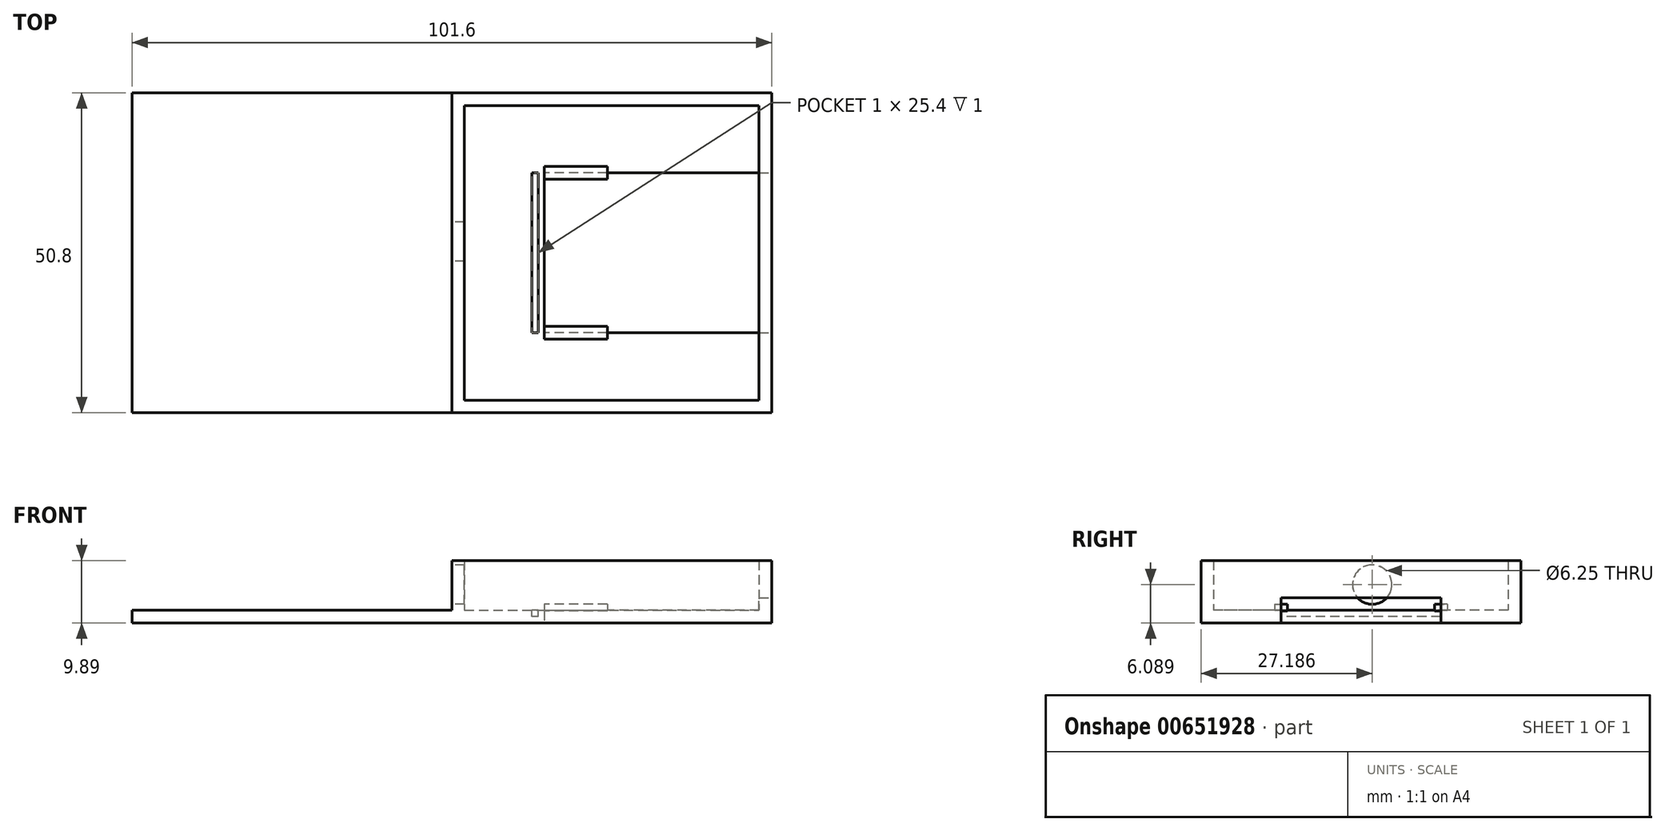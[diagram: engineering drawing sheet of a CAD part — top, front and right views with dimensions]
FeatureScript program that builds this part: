
annotation { "Feature Type Name" : "Feature", "Feature Type Description" : "" }
export const myFeature = defineFeature(function(context is Context, id is Id, definition is map)
    precondition{}
    {
        {
            var Q0;
            Q0=qCreatedBy(makeId("Top.planeOp"),FACE);
            var sketch = newSketch(context, id + "F0", { "sketchPlane" : qUnion([Q0])});
            skLineSegment(sketch, "E0.bottom", {"start": v(-50.8, 25.4) * mm, "end": v(50.8, 25.4) * mm});
            skLineSegment(sketch, "E0.top", {"start": v(-50.8, -25.4) * mm, "end": v(50.8, -25.4) * mm});
            skLineSegment(sketch, "E0.right", {"start": v(50.8, 25.4) * mm, "end": v(50.8, 12.7) * mm});
            skPoint(sketch, "E1.start.orphan", {"position": v(-50.8, 0) * mm});
            skLineSegment(sketch, "E2", {"start": v(-50.8, 25.4) * mm, "end": v(-50.8, -25.4) * mm});
            skLineSegment(sketch, "E3", {"start": v(50.8, 12.7) * mm, "end": v(14.7, 12.7) * mm});
            skLineSegment(sketch, "E4.MirrorCS", {"start": v(50.8, -12.7) * mm, "end": v(14.7, -12.7) * mm});
            skLineSegment(sketch, "E5.trimOffspring", {"start": v(50.8, -12.7) * mm, "end": v(50.8, -25.4) * mm});
            skLineSegment(sketch, "E6", {"start": v(14.7, -12.7) * mm, "end": v(14.7, 12.7) * mm});
            skSolve(sketch);
        }
        {
            var Q0;
            Q0 = qSketchRegion(id + "F0", true);
            extrude(context, id + "F1", {"entities" : qUnion([Q0]), "depth" : 2 * mm, "offsetDistance" : 25.4 * mm});
        }
        {
            var Q0;
            Q0=makeQuery(id+"F1.opExtrude","CAP_FACE",FACE,{"disambiguationData":[OSD([sQuery(id+"F0.wireOp",EDGE,"E0.bottom"),sQuery(id+"F0.wireOp",EDGE,"E0.top"),sQuery(id+"F0.wireOp",EDGE,"E0.right"),sQuery(id+"F0.wireOp",EDGE,"E2")])],"isStart":false});
            var sketch = newSketch(context, id + "F2", { "sketchPlane" : qUnion([Q0])});
            skLineSegment(sketch, "E7", {"start": v(50.8, 25.4) * mm, "end": v(0, 25.4) * mm});
            skLineSegment(sketch, "E8", {"start": v(2, 23.4) * mm, "end": v(48.8, 23.4) * mm});
            skLineSegment(sketch, "E9", {"start": v(48.8, 23.4) * mm, "end": v(48.8, -23.4) * mm});
            skLineSegment(sketch, "E10", {"start": v(48.8, -23.4) * mm, "end": v(2, -23.4) * mm});
            skLineSegment(sketch, "E11", {"start": v(0, -25.4) * mm, "end": v(50.8, -25.4) * mm});
            skLineSegment(sketch, "E12", {"start": v(50.8, -25.4) * mm, "end": v(50.8, 25.4) * mm});
            skLineSegment(sketch, "E13", {"start": v(0, 25.4) * mm, "end": v(0, -25.4) * mm});
            skLineSegment(sketch, "E14.0", {"start": v(2, 23.4) * mm, "end": v(2, -23.4) * mm});
            skPoint(sketch, "E15.orphan", {"position": v(0, -23.4) * mm});
            skSolve(sketch);
        }
        {
            var Q0;
            Q0 = qSketchRegion(id + "F2", true);
            extrude(context, id + "F3", {"entities" : qUnion([Q0]), "operationType" : NewBodyOperationType.ADD, "depth" : 8.9 * mm, "offsetDistance" : 25.4 * mm});
        }
        {
            var Q0;
            Q0=makeQuery(id+"F3.opExtrude","SWEPT_FACE",FACE,{"disambiguationData":[OSD([sQuery(id+"F2.wireOp",EDGE,"E13")])]});
            var sketch = newSketch(context, id + "F4", { "sketchPlane" : qUnion([Q0])});
            skCircle(sketch, "E16", {"center": v(-1.79, 6.09) * mm, "radius": 3.13 * mm});
            skSolve(sketch);
        }
        {
            var Q0;
            Q0 = qSketchRegion(id + "F4", true);
            extrude(context, id + "F5", {"entities" : qUnion([Q0]), "operationType" : NewBodyOperationType.REMOVE, "oppositeDirection" : true, "depth" : 25.4 * mm, "offsetDistance" : 25.4 * mm});
        }
        {
            var Q0;
            Q0=makeQuery(id+"F3.boolean.opBoolean","MERGE",FACE,{"derivedFrom":[makeQuery(id+"F1.opExtrude","SWEPT_FACE",FACE,{"disambiguationData":[OSD([sQuery(id+"F0.wireOp",EDGE,"E0.right")])]}),makeQuery(id+"F1.opExtrude","SWEPT_FACE",FACE,{"disambiguationData":[OSD([sQuery(id+"F0.wireOp",EDGE,"E5.trimOffspring")])]}),makeQuery(id+"F3.opExtrude","SWEPT_FACE",FACE,{"disambiguationData":[OSD([sQuery(id+"F2.wireOp",EDGE,"E12")])]})]});
            var sketch = newSketch(context, id + "F6", { "sketchPlane" : qUnion([Q0])});
            skLineSegment(sketch, "E17.bottom", {"start": v(12.7, 2) * mm, "end": v(-12.7, 2) * mm});
            skLineSegment(sketch, "E17.top", {"start": v(12.7, 4) * mm, "end": v(-12.7, 4) * mm});
            skLineSegment(sketch, "E17.left", {"start": v(12.7, 2) * mm, "end": v(12.7, 4) * mm});
            skLineSegment(sketch, "E17.right", {"start": v(-12.7, 2) * mm, "end": v(-12.7, 4) * mm});
            skSolve(sketch);
        }
        {
            var Q0;
            Q0 = qSketchRegion(id + "F6", true);
            extrude(context, id + "F7", {"entities" : qUnion([Q0]), "operationType" : NewBodyOperationType.REMOVE, "oppositeDirection" : true, "depth" : 25.4 * mm, "offsetDistance" : 25.4 * mm});
        }
        {
            var Q0;
            Q0=makeQuery(id+"F3.opExtrude","CAP_FACE",FACE,{"disambiguationData":[OSD([sQuery(id+"F2.wireOp",EDGE,"E7"),sQuery(id+"F2.wireOp",EDGE,"E8"),sQuery(id+"F2.wireOp",EDGE,"E9"),sQuery(id+"F2.wireOp",EDGE,"E10"),sQuery(id+"F2.wireOp",EDGE,"E11"),sQuery(id+"F2.wireOp",EDGE,"E12"),sQuery(id+"F2.wireOp",EDGE,"E13"),sQuery(id+"F2.wireOp",EDGE,"E14.0")])],"isStart":false});
            var sketch = newSketch(context, id + "F8", { "sketchPlane" : qUnion([Q0])});
            skLineSegment(sketch, "E18.bottom", {"start": v(0, 25.4) * mm, "end": v(50.8, 25.4) * mm});
            skLineSegment(sketch, "E18.top", {"start": v(0, -25.4) * mm, "end": v(50.8, -25.4) * mm});
            skLineSegment(sketch, "E18.left", {"start": v(0, 25.4) * mm, "end": v(0, -25.4) * mm});
            skLineSegment(sketch, "E18.right", {"start": v(50.8, 25.4) * mm, "end": v(50.8, -25.4) * mm});
            skSolve(sketch);
        }
        {
            var Q0;
            Q0 = qSketchRegion(id + "F8", true);
            extrude(context, id + "F9", {"entities" : qUnion([Q0]), "operationType" : NewBodyOperationType.REMOVE, "oppositeDirection" : true, "depth" : 1 * mm, "offsetDistance" : 25.4 * mm});
        }
        {
            var Q0;
            {var subQ4=sQuery(id+"F0.wireOp",EDGE,"E6");var subQ5=sQuery(id+"F0.wireOp",EDGE,"E4.MirrorCS");var subQ6=sQuery(id+"F0.wireOp",EDGE,"E3");Q0=makeQuery(id+"F3.boolean.opBoolean","SPLIT",FACE,{"disambiguationData":[TD([makeQuery(id+"F1.opExtrude","SWEPT_FACE",FACE,{"disambiguationData":[OSD([subQ6])]})])],"derivedFrom":makeQuery(id+"F1.opExtrude","CAP_FACE",FACE,{"disambiguationData":[OSD([sQuery(id+"F0.wireOp",EDGE,"E0.bottom"),sQuery(id+"F0.wireOp",EDGE,"E0.top"),sQuery(id+"F0.wireOp",EDGE,"E0.right"),sQuery(id+"F0.wireOp",EDGE,"E2"),subQ6,subQ5,sQuery(id+"F0.wireOp",EDGE,"E5.trimOffspring"),subQ4])],"isStart":false})});}
            var sketch = newSketch(context, id + "F10", { "sketchPlane" : qUnion([Q0])});
            skLineSegment(sketch, "E19", {"start": v(13.7, -12.7) * mm, "end": v(12.7, -12.7) * mm});
            skLineSegment(sketch, "E20", {"start": v(12.7, -12.7) * mm, "end": v(12.7, 12.7) * mm});
            skLineSegment(sketch, "E21", {"start": v(12.7, 12.7) * mm, "end": v(13.7, 12.7) * mm});
            skLineSegment(sketch, "E22", {"start": v(13.7, 12.7) * mm, "end": v(13.7, -12.7) * mm});
            skSolve(sketch);
        }
        {
            var Q0;
            Q0 = qSketchRegion(id + "F10", true);
            extrude(context, id + "F11", {"entities" : qUnion([Q0]), "operationType" : NewBodyOperationType.REMOVE, "oppositeDirection" : true, "depth" : 1 * mm, "offsetDistance" : 25.4 * mm});
        }
        {
            var Q0;
            {var subQ4=sQuery(id+"F0.wireOp",EDGE,"E6");var subQ5=sQuery(id+"F0.wireOp",EDGE,"E4.MirrorCS");var subQ6=sQuery(id+"F0.wireOp",EDGE,"E3");Q0=makeQuery(id+"F3.boolean.opBoolean","SPLIT",FACE,{"disambiguationData":[TD([makeQuery(id+"F1.opExtrude","SWEPT_FACE",FACE,{"disambiguationData":[OSD([subQ6])]})])],"derivedFrom":makeQuery(id+"F1.opExtrude","CAP_FACE",FACE,{"disambiguationData":[OSD([sQuery(id+"F0.wireOp",EDGE,"E0.bottom"),sQuery(id+"F0.wireOp",EDGE,"E0.top"),sQuery(id+"F0.wireOp",EDGE,"E0.right"),sQuery(id+"F0.wireOp",EDGE,"E2"),subQ6,subQ5,sQuery(id+"F0.wireOp",EDGE,"E5.trimOffspring"),subQ4])],"isStart":false})});}
            var sketch = newSketch(context, id + "F12", { "sketchPlane" : qUnion([Q0])});
            skLineSegment(sketch, "E23.bottom", {"start": v(24.7, -13.7) * mm, "end": v(14.7, -13.7) * mm});
            skLineSegment(sketch, "E23.top", {"start": v(24.7, -11.7) * mm, "end": v(14.7, -11.7) * mm});
            skLineSegment(sketch, "E23.left", {"start": v(24.7, -13.7) * mm, "end": v(24.7, -11.7) * mm});
            skLineSegment(sketch, "E23.right", {"start": v(14.7, -13.7) * mm, "end": v(14.7, -11.7) * mm});
            skLineSegment(sketch, "E24.MirrorCS", {"start": v(24.7, 11.7) * mm, "end": v(14.7, 11.7) * mm});
            skLineSegment(sketch, "E25.MirrorCS", {"start": v(14.7, 13.7) * mm, "end": v(14.7, 11.7) * mm});
            skLineSegment(sketch, "E26.MirrorCS", {"start": v(24.7, 13.7) * mm, "end": v(14.7, 13.7) * mm});
            skLineSegment(sketch, "E27.MirrorCS", {"start": v(24.7, 13.7) * mm, "end": v(24.7, 11.7) * mm});
            skSolve(sketch);
        }
        {
            var Q0;
            Q0 = qSketchRegion(id + "F12", true);
            extrude(context, id + "F13", {"entities" : qUnion([Q0]), "operationType" : NewBodyOperationType.ADD, "depth" : 1 * mm, "offsetDistance" : 25.4 * mm, "hasSecondDirection" : true, "secondDirectionOppositeDirection" : true, "secondDirectionDepth" : .1 * mm});
        }
    });
